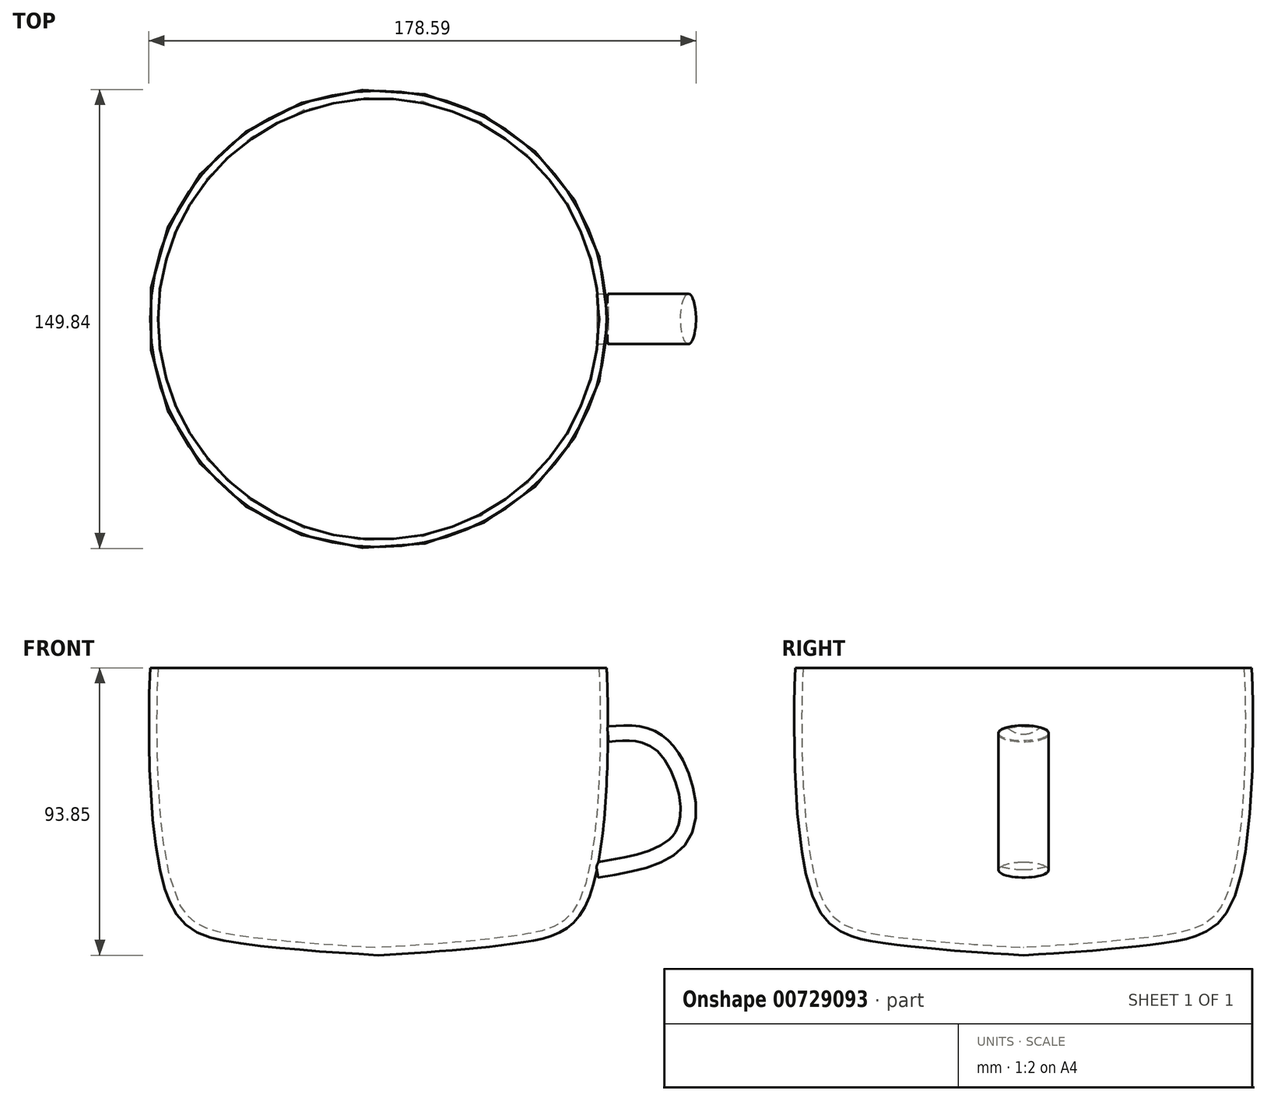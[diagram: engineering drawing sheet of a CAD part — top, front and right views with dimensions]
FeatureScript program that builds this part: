
annotation { "Feature Type Name" : "Feature", "Feature Type Description" : "" }
export const myFeature = defineFeature(function(context is Context, id is Id, definition is map)
    precondition{}
    {
        {
            var Q0;
            Q0=qCreatedBy(makeId("Front.planeOp"),FACE);
            var sketch = newSketch(context, id + "F0", { "sketchPlane" : qUnion([Q0])});
            skFitSpline(sketch, "E0", {"points": [v(74.5, 93.85) * mm, v(68.73, 18.78) * mm, v(47.45, 4.26) * mm, v(0, 0) * mm], "startDerivative": vector(4.73, -88.68) * mm, "endDerivative": vector(-132.93, -8.23) * mm});
            skLineSegment(sketch, "E1", {"start": v(0, 0) * mm, "end": v(0, 93.85) * mm});
            skLineSegment(sketch, "E2", {"start": v(74.5, 93.85) * mm, "end": v(0, 93.85) * mm});
            skSolve(sketch);
        }
        {
            var Q0;
            Q0=makeQuery(id+"F0.imprint","IMPRINT",FACE,{"disambiguationData":[TD([[makeQuery(id+"F0.imprint","IMPRINT",EDGE,{"derivedFrom":sQuery(id+"F0.wireOp",EDGE,"E0")}),-1.0]])]});
            var Q1;
            Q1=sQuery(id+"F0.wireOp",EDGE,"E1");
            revolve(context, id + "F1", {"surfaceOperationType" : NewSurfaceOperationType.NEW, "entities" : qUnion([Q0]), "axis" : qUnion([Q1]), "revolveType" : RevolveType.FULL});
        }
        {
            var Q0;
            Q0=makeQuery(id+"F1.opRevolve","SWEPT_FACE",FACE,{"disambiguationData":[OSD([sQuery(id+"F0.wireOp",EDGE,"E2")])]});
            shell(context, id + "F2", {"entities" : qUnion([Q0]), "thickness" : 2.5 * mm});
        }
        {
            var Q0;
            Q0=qCreatedBy(makeId("Front.planeOp"),FACE);
            var sketch = newSketch(context, id + "F3", { "sketchPlane" : qUnion([Q0])});
            skFitSpline(sketch, "E3", {"points": [v(0, 0) * mm, v(-14.8, 0.92) * mm, v(-47.88, 2.99) * mm, v(-76.5, 11.52) * mm, v(-75.16, 81.44) * mm, v(-74.5, 93.85) * mm], "construction": true});
            skFitSpline(sketch, "E4", {"points": [v(74.5, 93.85) * mm, v(75.16, 81.44) * mm, v(76.5, 11.52) * mm, v(47.88, 2.99) * mm, v(14.8, 0.92) * mm, v(0, 0) * mm], "construction": true});
            skFitSpline(sketch, "E5", {"points": [v(74.9, 72.18) * mm, v(92.52, 68.67) * mm, v(99.88, 40.32) * mm, v(71.32, 27.83) * mm], "startDerivative": vector(67.77, 5.93) * mm, "endDerivative": vector(-101.6, -16.47) * mm});
            skSolve(sketch);
        }
        {
            var Q0;
            Q0=sQuery(id+"F3.wireOp",VERTEX,"E5.0.internal");
            var Q1;
            Q1=sQuery(id+"F3.wireOp",EDGE,"E5");
            cPlane(context, id + "F4", {"entities" : qUnion([Q0, Q1]), "cplaneType" : CPlaneType.CURVE_POINT, "offset" : 25 * mm, "width" : 150 * mm, "height" : 150 * mm});
        }
        {
            var Q0;
            Q0=qCreatedBy(id+"F4.planeOp",FACE);
            var sketch = newSketch(context, id + "F5", { "sketchPlane" : qUnion([Q0])});
            skEllipse(sketch, "E6", {"center": v(0, 65.38) * mm, "majorRadius": 8.21 * mm, "minorRadius": 2.5 * mm, "majorAxis": v(1, 0)});
            skSolve(sketch);
        }
        {
            var Q0;
            Q0=makeQuery(id+"F5.imprint","IMPRINT",FACE,{"disambiguationData":[TD([[makeQuery(id+"F5.imprint","IMPRINT",EDGE,{"derivedFrom":sQuery(id+"F5.wireOp",EDGE,"E6")}),1.0]])]});
            var Q1;
            Q1=sQuery(id+"F3.wireOp",EDGE,"E5");
            sweep(context, id + "F6", {"operationType" : NewBodyOperationType.ADD, "profiles" : qUnion([Q0]), "path" : qUnion([Q1])});
        }
    });
